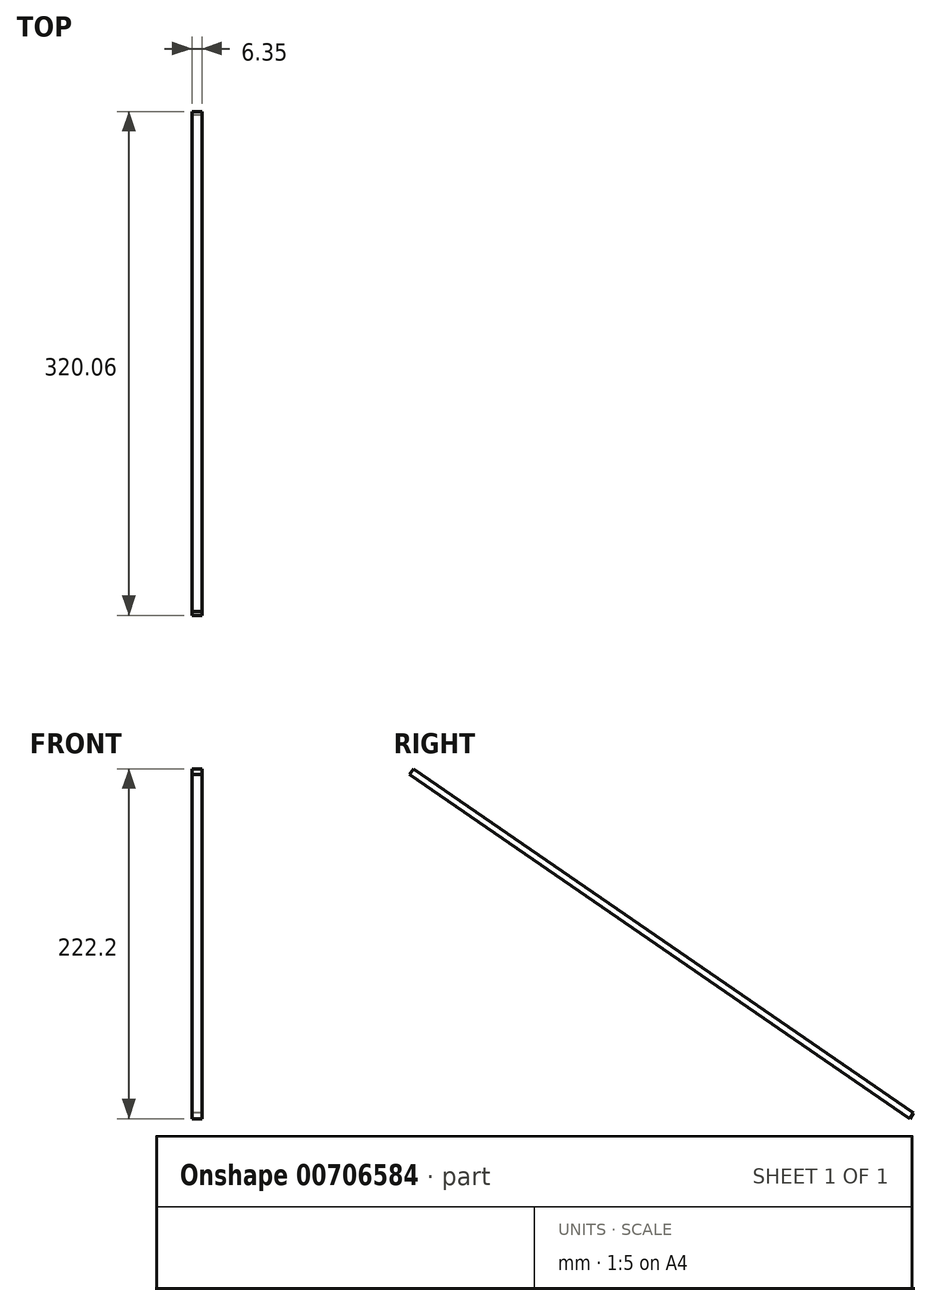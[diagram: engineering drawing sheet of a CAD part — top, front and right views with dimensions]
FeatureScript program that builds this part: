
annotation { "Feature Type Name" : "Feature", "Feature Type Description" : "" }
export const myFeature = defineFeature(function(context is Context, id is Id, definition is map)
    precondition{}
    {
        {
            var Q0;
            Q0=qCreatedBy(makeId("Right.planeOp"),FACE);
            var sketch = newSketch(context, id + "F0", { "sketchPlane" : qUnion([Q0])});
            skLineSegment(sketch, "E0", {"start": v(0, 0) * mm, "end": v(-114.08, 78.53) * mm});
            skLineSegment(sketch, "E1", {"start": v(-114.08, 78.53) * mm, "end": v(-116.49, 75.04) * mm});
            skLineSegment(sketch, "E2", {"start": v(-116.49, 75.04) * mm, "end": v(-2.34, -3.54) * mm});
            skLineSegment(sketch, "E3", {"start": v(-2.34, -3.54) * mm, "end": v(0, 0) * mm});
            skSolve(sketch);
        }
        {
            var Q0;
            Q0 = qSketchRegion(id + "F0", true);
            extrude(context, id + "F1", {"entities" : qUnion([Q0]), "depth" : 6.35 * mm, "offsetDistance" : 25.4 * mm});
        }
        {
            var Q0;
            Q0=makeQuery(id+"F1.opExtrude","SWEPT_FACE",FACE,{"disambiguationData":[OSD([sQuery(id+"F0.wireOp",EDGE,"E1")])]});
            extrude(context, id + "F2", {"entities" : qUnion([Q0]), "operationType" : NewBodyOperationType.ADD, "depth" : 247.14 * mm, "offsetDistance" : 25.4 * mm});
        }
    });
